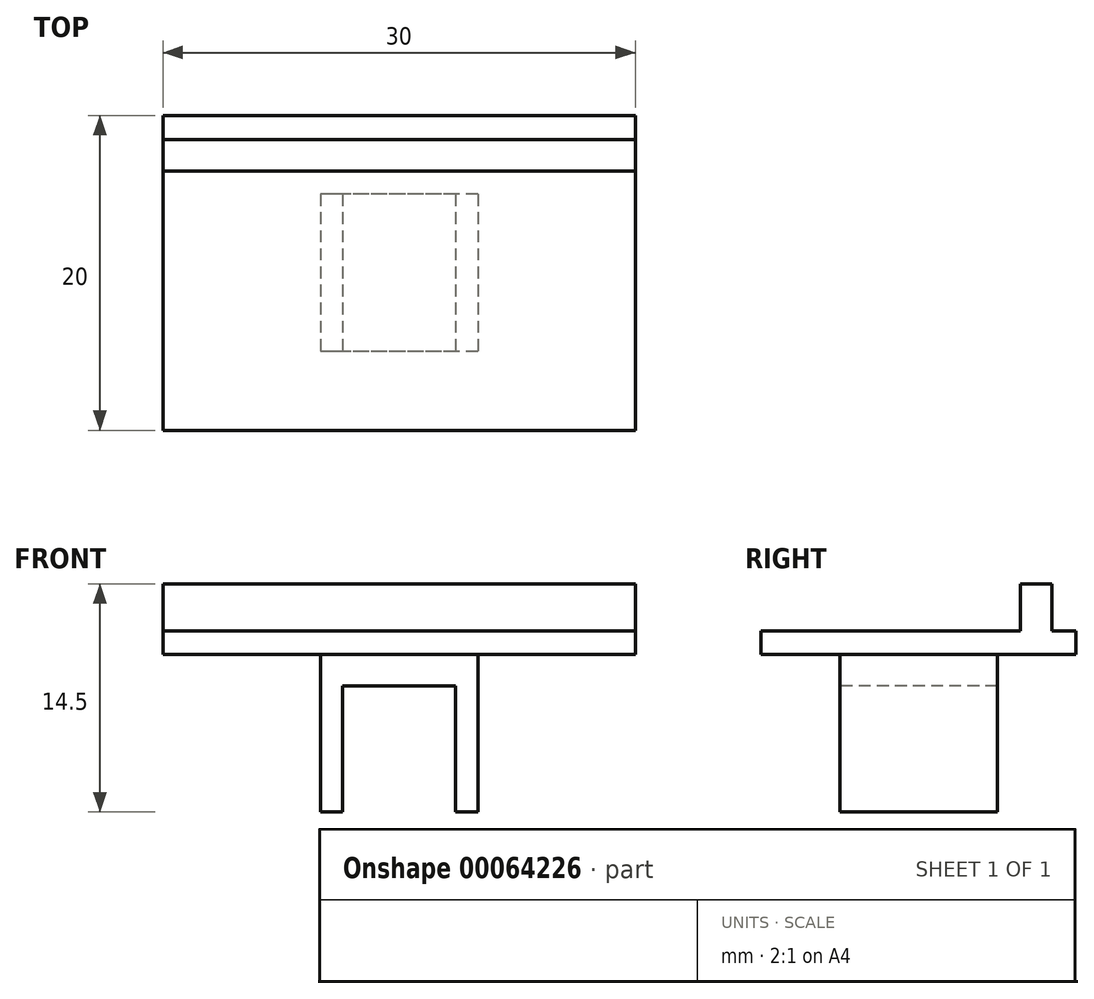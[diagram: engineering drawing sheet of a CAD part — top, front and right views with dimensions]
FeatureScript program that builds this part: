
annotation { "Feature Type Name" : "Feature", "Feature Type Description" : "" }
export const myFeature = defineFeature(function(context is Context, id is Id, definition is map)
    precondition{}
    {
        {
            var Q0;
            Q0=qCreatedBy(makeId("Top.planeOp"),FACE);
            var sketch = newSketch(context, id + "F0", { "sketchPlane" : qUnion([Q0])});
            skLineSegment(sketch, "E0.rect.bottom", {"start": v(15, -10) * mm, "end": v(-15, -10) * mm});
            skLineSegment(sketch, "E0.rect.top", {"start": v(15, 10) * mm, "end": v(-15, 10) * mm});
            skLineSegment(sketch, "E0.rect.left", {"start": v(15, -10) * mm, "end": v(15, 10) * mm});
            skLineSegment(sketch, "E0.rect.right", {"start": v(-15, -10) * mm, "end": v(-15, 10) * mm});
            skPoint(sketch, "E0.rect.middle", {"position": v(0, 0) * mm});
            skSolve(sketch);
        }
        {
            var Q0;
            Q0=makeQuery(id+"F0.imprint","IMPRINT",FACE,{"disambiguationData":[TD([[makeQuery(id+"F0.imprint","IMPRINT",EDGE,{"derivedFrom":sQuery(id+"F0.wireOp",EDGE,"E0.rect.bottom")}),-1.0]])]});
            extrude(context, id + "F1", {"entities" : qUnion([Q0]), "depth" : 1.5 * mm});
        }
        {
            var Q0;
            Q0=makeQuery(id+"F1.opExtrude","CAP_FACE",FACE,{"disambiguationData":[OSD([sQuery(id+"F0.wireOp",EDGE,"E0.rect.bottom"),sQuery(id+"F0.wireOp",EDGE,"E0.rect.top"),sQuery(id+"F0.wireOp",EDGE,"E0.rect.left"),sQuery(id+"F0.wireOp",EDGE,"E0.rect.right")])],"isStart":false});
            var sketch = newSketch(context, id + "F2", { "sketchPlane" : qUnion([Q0])});
            skLineSegment(sketch, "E1.bottom", {"start": v(-15, 8.47) * mm, "end": v(15, 8.47) * mm});
            skLineSegment(sketch, "E1.top", {"start": v(-15, 6.47) * mm, "end": v(15, 6.47) * mm});
            skLineSegment(sketch, "E1.left", {"start": v(-15, 8.47) * mm, "end": v(-15, 6.47) * mm});
            skLineSegment(sketch, "E1.right", {"start": v(15, 8.47) * mm, "end": v(15, 6.47) * mm});
            skSolve(sketch);
        }
        {
            var Q0;
            Q0=makeQuery(id+"F2.imprint","IMPRINT",FACE,{"disambiguationData":[TD([[makeQuery(id+"F2.imprint","IMPRINT",EDGE,{"derivedFrom":sQuery(id+"F2.wireOp",EDGE,"E1.bottom")}),-1.0]])]});
            extrude(context, id + "F3", {"entities" : qUnion([Q0]), "operationType" : NewBodyOperationType.ADD, "depth" : 3 * mm});
        }
        {
            var Q0;
            Q0=makeQuery(id+"F1.opExtrude","CAP_FACE",FACE,{"disambiguationData":[OSD([sQuery(id+"F0.wireOp",EDGE,"E0.rect.bottom"),sQuery(id+"F0.wireOp",EDGE,"E0.rect.top"),sQuery(id+"F0.wireOp",EDGE,"E0.rect.left"),sQuery(id+"F0.wireOp",EDGE,"E0.rect.right")])],"isStart":true});
            var sketch = newSketch(context, id + "F4", { "sketchPlane" : qUnion([Q0])});
            skLineSegment(sketch, "E2", {"start": v(-15, 0) * mm, "end": v(15, 0) * mm});
            skPoint(sketch, "E3", {"position": v(-5, 0) * mm});
            skPoint(sketch, "E4", {"position": v(0, 0) * mm});
            skPoint(sketch, "E5", {"position": v(5, 0) * mm});
            skLineSegment(sketch, "E6.rect.bottom", {"start": v(5, -5) * mm, "end": v(-5, -5) * mm});
            skLineSegment(sketch, "E6.rect.top", {"start": v(5, 5) * mm, "end": v(-5, 5) * mm});
            skLineSegment(sketch, "E6.rect.left", {"start": v(5, -5) * mm, "end": v(5, 5) * mm});
            skLineSegment(sketch, "E6.rect.right", {"start": v(-5, -5) * mm, "end": v(-5, 5) * mm});
            skSolve(sketch);
        }
        {
            var Q0;
            {var subQ5=sQuery(id+"F4.wireOp",EDGE,"E6.rect.top");Q0=makeQuery(id+"F4.imprint","IMPRINT",FACE,{"disambiguationData":[TD([[makeQuery(id+"F4.imprint","IMPRINT",EDGE,{"derivedFrom":subQ5}),1.0]])]});}
            var Q1;
            {var subQ5=sQuery(id+"F4.wireOp",EDGE,"E6.rect.bottom");Q1=makeQuery(id+"F4.imprint","IMPRINT",FACE,{"disambiguationData":[TD([[makeQuery(id+"F4.imprint","IMPRINT",EDGE,{"derivedFrom":subQ5}),-1.0]])]});}
            extrude(context, id + "F5", {"entities" : qUnion([Q0, Q1]), "operationType" : NewBodyOperationType.ADD, "depth" : 10 * mm});
        }
        {
            var Q0;
            Q0=makeQuery(id+"F5.opExtrude","CAP_FACE",FACE,{"disambiguationData":[OSD([sQuery(id+"F4.wireOp",EDGE,"E6.rect.bottom"),sQuery(id+"F4.wireOp",EDGE,"E6.rect.top"),sQuery(id+"F4.wireOp",EDGE,"E6.rect.left"),sQuery(id+"F4.wireOp",EDGE,"E6.rect.right")])],"isStart":false});
            var sketch = newSketch(context, id + "F6", { "sketchPlane" : qUnion([Q0])});
            skLineSegment(sketch, "E7.rect.bottom", {"start": v(3.58, -5) * mm, "end": v(-3.58, -5) * mm});
            skLineSegment(sketch, "E7.rect.top", {"start": v(3.58, 5) * mm, "end": v(-3.58, 5) * mm});
            skLineSegment(sketch, "E7.rect.left", {"start": v(3.58, -5) * mm, "end": v(3.58, 5) * mm});
            skLineSegment(sketch, "E7.rect.right", {"start": v(-3.58, -5) * mm, "end": v(-3.58, 5) * mm});
            skPoint(sketch, "E7.rect.middle", {"position": v(0, 0) * mm});
            skSolve(sketch);
        }
        {
            var Q0;
            Q0=makeQuery(id+"F6.imprint","IMPRINT",FACE,{"disambiguationData":[TD([[makeQuery(id+"F6.imprint","IMPRINT",EDGE,{"derivedFrom":sQuery(id+"F6.wireOp",EDGE,"E7.rect.bottom")}),-1.0]])]});
            extrude(context, id + "F7", {"entities" : qUnion([Q0]), "operationType" : NewBodyOperationType.REMOVE, "oppositeDirection" : true, "depth" : 8 * mm});
        }
    });
